# Revit family: ed
name_source: partatom
category: Plumbing Fixtures
revit_build: Autodesk Revit 2018 (Build: 20190510_1515(x64)
units: mm (PartAtom-declared; Revit-internal decimal feet)

## family parameters
Always vertical = No
Cut with Voids When Loaded = No
OmniClass Number = 23.31.15.00
OmniClass Title = Bathtubs
Part Type = Normal
Room Calculation Point = No
Round Connector Dimension = Use Diameter
Shared = No
Work Plane-Based = Yes

## types (1)
- D-Code Bathtub, 1700x700 mm - 700098
    BIMobject category = Bath & Spas
    Connector Description = Water outlet
    Default Elevation = 1219.2 mm  [stored 4 ft]
    Description = Duravit D-Code Bathtub, 1700x700 mm Interior colour White, drop-in, Sanitary acrylic, Rectangular, Number of backrests: 1, Overflow - 700098000000000
    Design country = Germany
    ETIM classification = EC011609 | Bath
    Edition number = 1
    IFC Classification = Sanitary Terminal
    Installation instructions = https://pro.duravit.com
    Main material = Duravit - Ceramic - 00 - White Alpin
    Manufacturer = Duravit
    Manufacturer country = Germany
    Manufacturer name = DURAVIT AG
    Masterformat 2014 Code = 22 41 19
    Masterformat 2014 Description = Residential Bathtubs
    Material main = Acrylic
    Metal material = Duravit - Metal - 10 - Chrome
    Model = D-Code Bathtub, 1700x700 mm - 700098
    OmniClass Code = 23-31 15 00
    OmniClass Description = Bathtubs
    Outlet Diameter = 50 mm
    Product Guid = fc9bf38c-b7a3-41b2-af0a-90087d86669f
    Product SKU = D-Code-Bathtub-1700x700-mm-700098
    Product certification = https://pro.duravit.com
    Product data url = https://bimobject.com
    Product family = Bathtubs & Wellbeing
    Product group = Bathtub
    Product name = D-Code Bathtub, 1700x700 mm - 700098
    Product url = http://pro.duravit.com
    QR code = https://bimobject.com
    Technical description = https://pro.duravit.com
    UNSPSC Code = 30181501
    URL = https://www.duravit.com
    Uniclass 2015 Code = Pr_40_20_06_08
    Uniclass 2015 Name = Baths
    Uniformat II Code = D2010
    Uniformat II Description = Plumbing Fixtures
    Weight Net (Kg) = 29
    Youtube clip = https://pro.duravit.com

note: [stored X ft] marks values corroborated as IEEE doubles in the binary element streams (Revit-internal decimal feet)

## geometry (parser evidence)
native form markers: Sweep x3
no freeform markers — native parametric forms only
